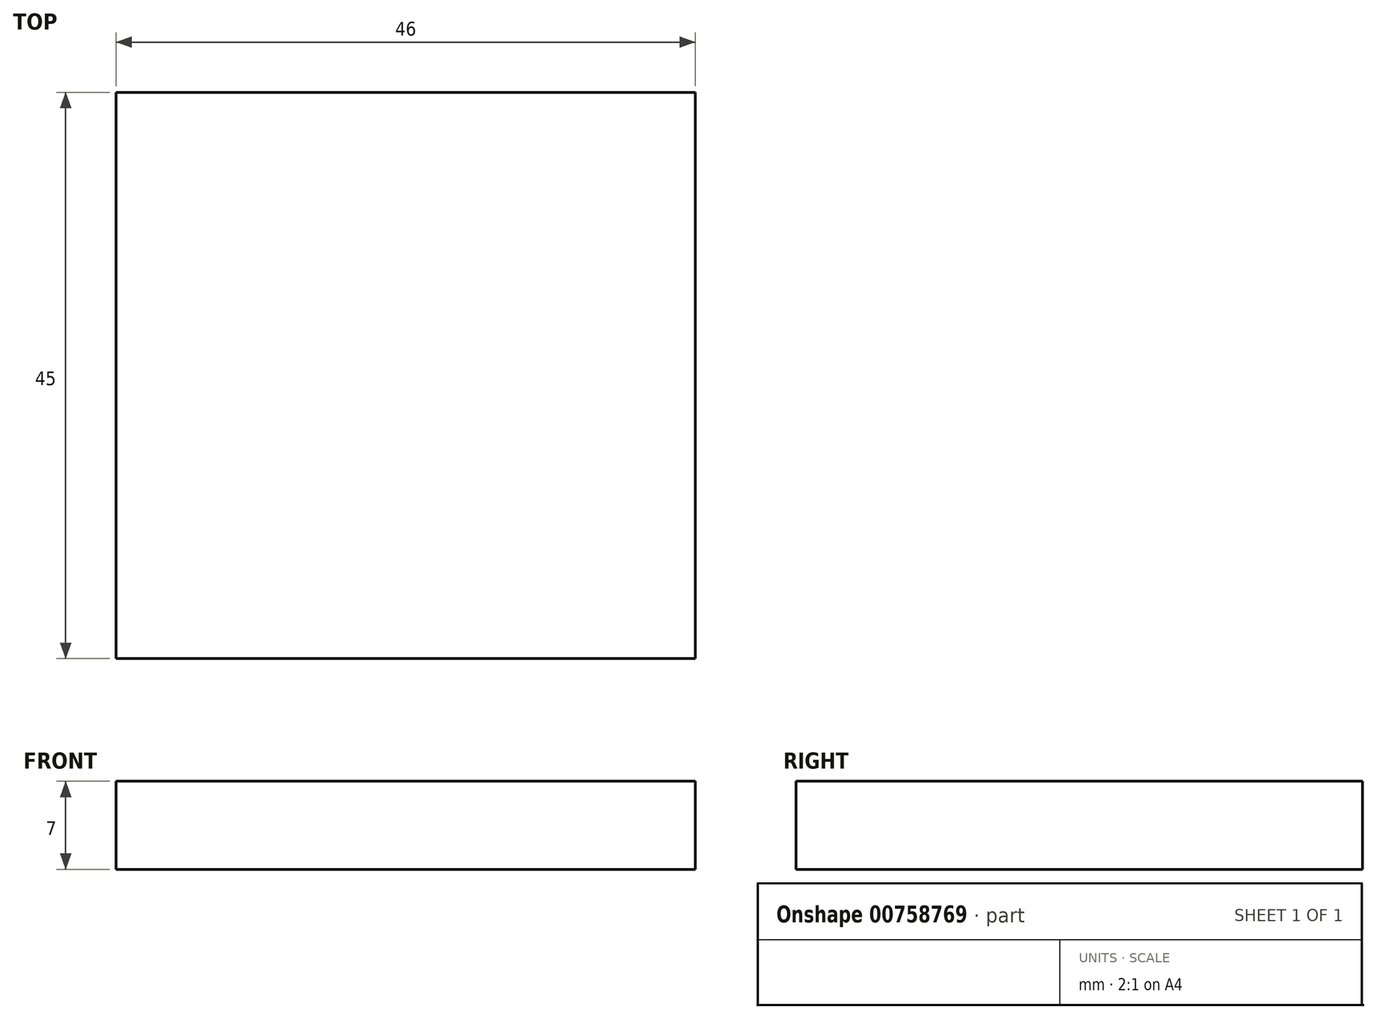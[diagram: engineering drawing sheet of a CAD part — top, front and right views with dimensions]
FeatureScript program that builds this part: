
annotation { "Feature Type Name" : "Feature", "Feature Type Description" : "" }
export const myFeature = defineFeature(function(context is Context, id is Id, definition is map)
    precondition{}
    {
        {
            var Q0;
            Q0=qCreatedBy(makeId("Front.planeOp"),FACE);
            var sketch = newSketch(context, id + "F0", { "sketchPlane" : qUnion([Q0])});
            skLineSegment(sketch, "E0.bottom", {"start": v(-23, 7) * mm, "end": v(23, 7) * mm});
            skLineSegment(sketch, "E0.top", {"start": v(-23, 0) * mm, "end": v(23, 0) * mm});
            skLineSegment(sketch, "E0.left", {"start": v(-23, 7) * mm, "end": v(-23, 0) * mm});
            skLineSegment(sketch, "E0.right", {"start": v(23, 7) * mm, "end": v(23, 0) * mm});
            skSolve(sketch);
        }
        {
            var Q0;
            Q0=makeQuery(id+"F0.imprint","IMPRINT",FACE,{"disambiguationData":[TD([[makeQuery(id+"F0.imprint","IMPRINT",EDGE,{"derivedFrom":sQuery(id+"F0.wireOp",EDGE,"E0.bottom")}),-1.0]])]});
            extrude(context, id + "F1", {"entities" : qUnion([Q0]), "oppositeDirection" : true, "depth" : 45 * mm, "offsetDistance" : 25 * mm});
        }
    });
